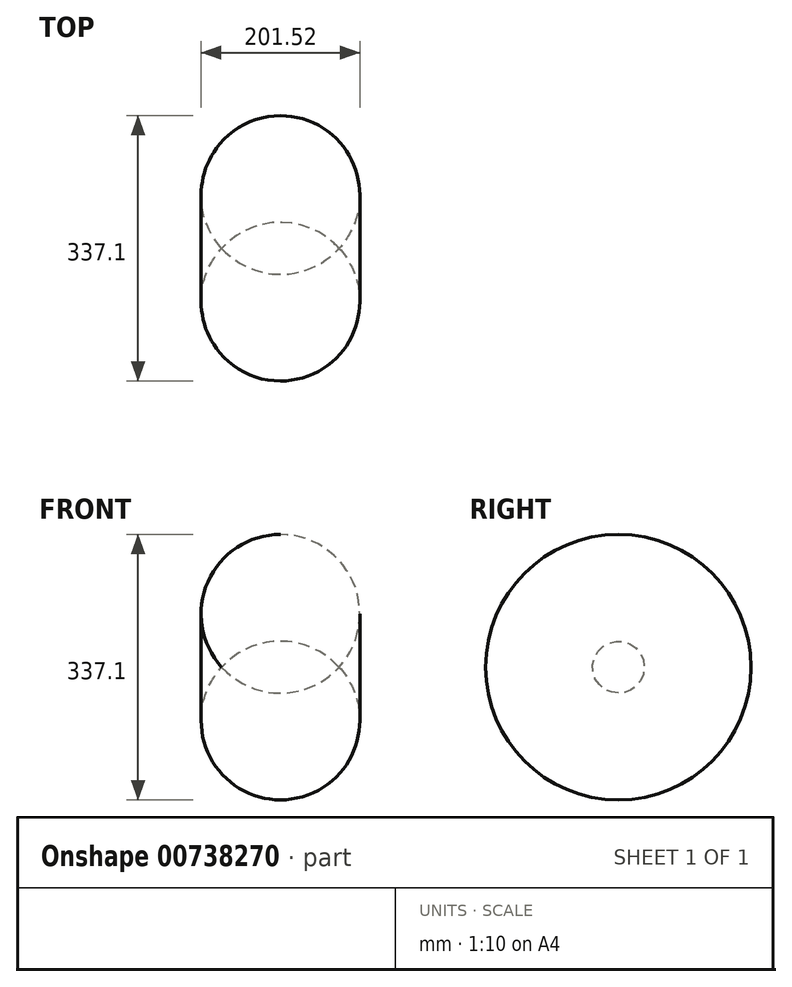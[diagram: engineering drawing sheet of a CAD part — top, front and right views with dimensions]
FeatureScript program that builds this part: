
annotation { "Feature Type Name" : "Feature", "Feature Type Description" : "" }
export const myFeature = defineFeature(function(context is Context, id is Id, definition is map)
    precondition{}
    {
        {
            var Q0;
            Q0=qCreatedBy(makeId("Front.planeOp"),FACE);
            var sketch = newSketch(context, id + "F0", { "sketchPlane" : qUnion([Q0])});
            skArc(sketch, "E0", {"start": v(74.1, 0) * mm, "mid": v(-0.43, 32.97) * mm, "end": v(-74.97, 0) * mm});
            skLineSegment(sketch, "E1", {"start": v(-74.97, 0) * mm, "end": v(74.1, 0) * mm});
            skSolve(sketch);
        }
        {
            var Q0;
            Q0=makeQuery(id+"F0.imprint","IMPRINT",FACE,{"disambiguationData":[TD([[makeQuery(id+"F0.imprint","IMPRINT",EDGE,{"derivedFrom":sQuery(id+"F0.wireOp",EDGE,"E0")}),1.0]])]});
            var Q1;
            Q1=sQuery(id+"F0.wireOp",EDGE,"E1");
            revolve(context, id + "F1", {"surfaceOperationType" : NewSurfaceOperationType.NEW, "entities" : qUnion([Q0]), "axis" : qUnion([Q1]), "revolveType" : RevolveType.FULL});
        }
    });
